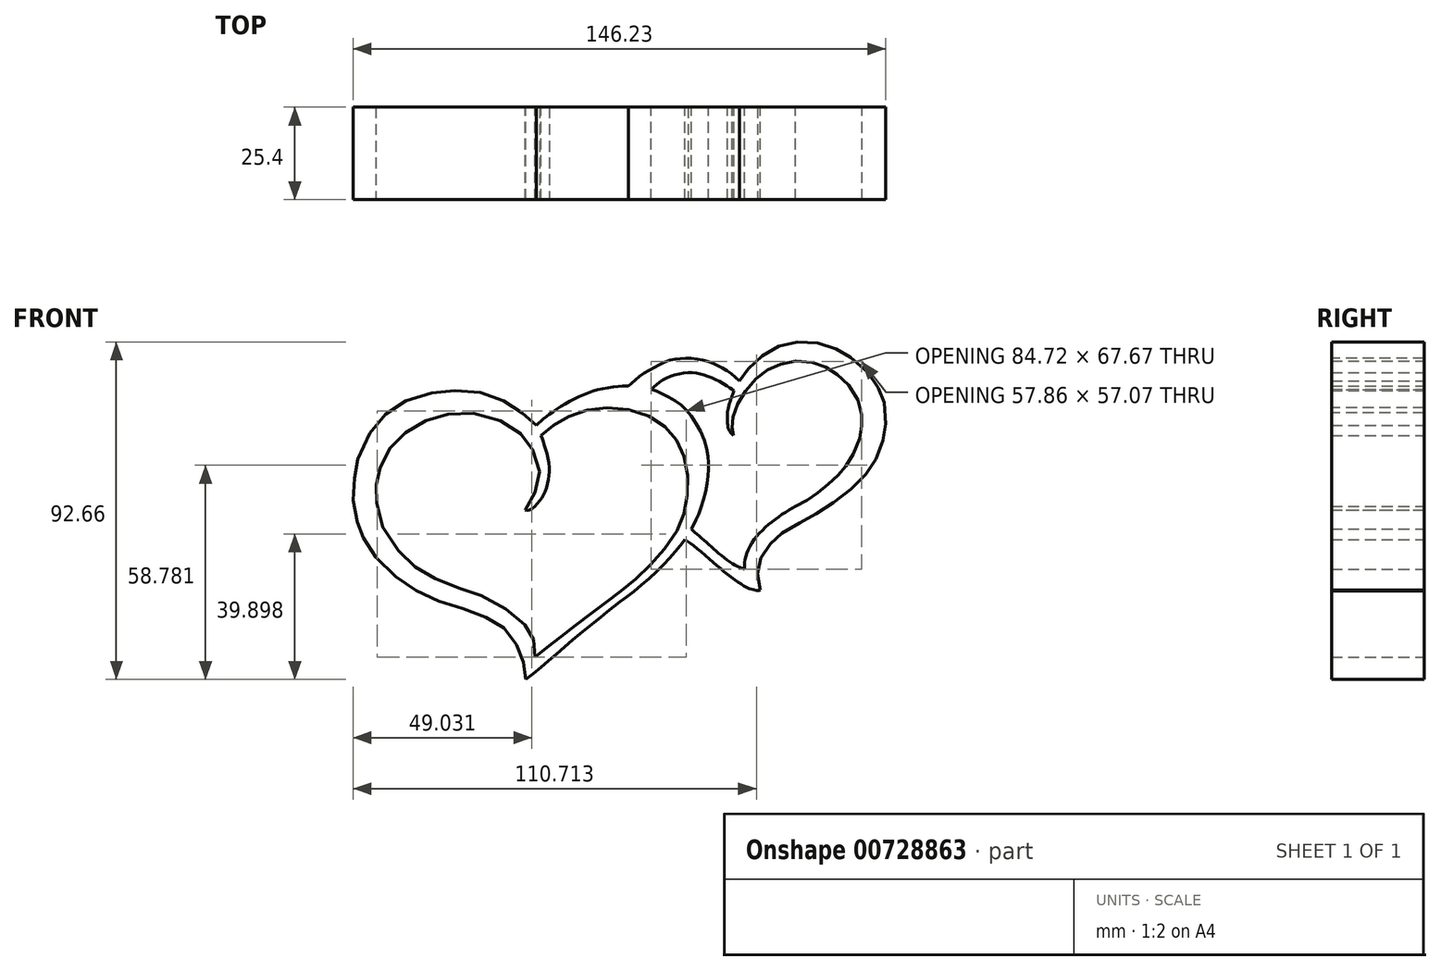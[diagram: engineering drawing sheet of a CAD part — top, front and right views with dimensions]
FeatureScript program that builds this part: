
annotation { "Feature Type Name" : "Feature", "Feature Type Description" : "" }
export const myFeature = defineFeature(function(context is Context, id is Id, definition is map)
    precondition{}
    {
        {
            var Q0;
            Q0=qCreatedBy(makeId("Front.planeOp"),FACE);
            var sketch = newSketch(context, id + "F0", { "sketchPlane" : qUnion([Q0])});
            skFitSpline(sketch, "E0", {"points": [v(-25.48, -6.95) * mm, v(-23.3, -3.15) * mm, v(-21.9, 1) * mm, v(-21.96, 6.21) * mm, v(-24.36, 11.07) * mm, v(-26.96, 14.24) * mm, v(-32.08, 17.5) * mm, v(-39.9, 19.6) * mm, v(-46.56, 19.44) * mm, v(-52.09, 17.95) * mm, v(-57.16, 15.21) * mm, v(-61.5, 11.53) * mm, v(-64.13, 7.75) * mm, v(-65.87, 2.87) * mm, v(-66.37, 0.47) * mm, v(-66.49, -2.24) * mm, v(-66, -7) * mm, v(-63.53, -13.83) * mm, v(-58.46, -20.09) * mm, v(-54.88, -23.15) * mm, v(-49.77, -26) * mm, v(-43.24, -28.5) * mm, v(-37.8, -30.35) * mm, v(-30.6, -34.2) * mm, v(-25.75, -38.22) * mm, v(-23.83, -40.9) * mm, v(-22.82, -44.16) * mm, v(-22.82, -47.34) * mm], "startDerivative": vector(68.52, 110.6) * mm, "endDerivative": vector(-7.66, -109.37) * mm});
            skFitSpline(sketch, "E1", {"points": [v(-22.82, -47.34) * mm, v(-18.93, -44.14) * mm, v(-13.48, -40) * mm, v(-7.44, -35.27) * mm, v(-1.64, -31) * mm, v(4.4, -26.15) * mm, v(10.3, -20.35) * mm, v(16.35, -12.19) * mm, v(18.6, -5.56) * mm, v(19.07, 2.49) * mm, v(17.41, 9.6) * mm, v(13.86, 15.03) * mm, v(7.23, 19.41) * mm, v(-2, 21.19) * mm, v(-10.29, 20) * mm, v(-16.91, 16.93) * mm, v(-21.17, 13.5) * mm], "startDerivative": vector(72.44, 60.92) * mm, "endDerivative": vector(-73.73, -66.23) * mm});
            skFitSpline(sketch, "E2", {"points": [v(-21.17, 13.5) * mm, v(-20.23, 10.77) * mm, v(-19.04, 5.68) * mm, v(-19.16, 1.3) * mm, v(-20.44, -2.66) * mm, v(-22.15, -5.12) * mm, v(-24.41, -6.92) * mm, v(-25.48, -6.95) * mm], "startDerivative": vector(6.78, -18.26) * mm, "endDerivative": vector(-12.06, 2.23) * mm});
            skFitSpline(sketch, "E3", {"points": [v(-22.49, 16.4) * mm, v(-21, 17.67) * mm, v(-18.66, 19.53) * mm, v(-14.77, 22.08) * mm, v(-9.66, 24.67) * mm, v(-4.8, 26.3) * mm, v(0.63, 27.06) * mm, v(2.8, 27.14) * mm], "startDerivative": vector(14.02, 12) * mm, "endDerivative": vector(17.69, 0.26) * mm});
            skFitSpline(sketch, "E4", {"points": [v(2.8, 27.14) * mm, v(4.52, 28.56) * mm, v(7.03, 30.62) * mm, v(10.05, 32.29) * mm, v(13.48, 34.02) * mm, v(16.24, 34.56) * mm, v(19.38, 34.73) * mm, v(22.94, 34.35) * mm, v(25.78, 33.52) * mm, v(28.38, 32.17) * mm, v(30.84, 30.63) * mm, v(33.23, 28.49) * mm], "startDerivative": vector(21.34, 17.25) * mm, "endDerivative": vector(25.3, -24.57) * mm});
            skFitSpline(sketch, "E5", {"points": [v(33.23, 28.49) * mm, v(34.32, 30) * mm, v(36.28, 32.51) * mm, v(38.88, 34.94) * mm, v(42.35, 37.33) * mm, v(45.7, 38.58) * mm, v(49.38, 39.21) * mm, v(53.78, 39.09) * mm, v(57.58, 38.2) * mm, v(61.1, 36.7) * mm, v(63.07, 35.53) * mm, v(67.25, 32.22) * mm, v(69.76, 29.16) * mm, v(71.69, 26.02) * mm, v(72.7, 23.46) * mm, v(73.32, 21.07) * mm, v(73.32, 15.2) * mm, v(72.86, 12.99) * mm, v(71.85, 9.55) * mm, v(70.05, 5.87) * mm, v(68.09, 3.1) * mm, v(65.28, 0) * mm, v(61.4, -3.26) * mm, v(57.42, -5.9) * mm, v(53.94, -8.12) * mm, v(50.64, -10) * mm, v(46.75, -12.14) * mm, v(43.9, -13.94) * mm, v(42.18, -15.66) * mm, v(40.22, -18.1) * mm, v(38.88, -20.9) * mm, v(38.33, -23.41) * mm, v(38.33, -25.93) * mm, v(39, -28.9) * mm], "startDerivative": vector(45.84, 63.78) * mm, "endDerivative": vector(29.25, -107.53) * mm});
            skFitSpline(sketch, "E6", {"points": [v(39, -28.9) * mm, v(38.47, -29.07) * mm, v(35.57, -28.3) * mm, v(33.64, -27.19) * mm, v(30.04, -24.57) * mm, v(26, -21.15) * mm, v(21.03, -16.96) * mm, v(18.28, -15.02) * mm], "startDerivative": vector(-6.74, -4.17) * mm, "endDerivative": vector(-17.62, 11.67) * mm});
            skFitSpline(sketch, "E7", {"points": [v(18.28, -15.02) * mm, v(14.97, -19.19) * mm, v(9.76, -24.52) * mm, v(3.25, -30.03) * mm, v(-1.42, -33.58) * mm, v(-6.16, -37.44) * mm, v(-11.66, -41.82) * mm, v(-18.94, -48.22) * mm, v(-25.38, -53.4) * mm], "startDerivative": vector(-28.94, -38.14) * mm, "endDerivative": vector(-47.2, -36.75) * mm});
            skFitSpline(sketch, "E8", {"points": [v(-25.38, -53.4) * mm, v(-25.4, -52.75) * mm, v(-26.15, -47.9) * mm, v(-27.6, -44.52) * mm, v(-29.98, -40.73) * mm, v(-33.17, -37.94) * mm, v(-37.9, -35.65) * mm, v(-44.12, -33.5) * mm, v(-50.49, -31.42) * mm, v(-56.46, -28.43) * mm, v(-61.58, -24.7) * mm, v(-67.3, -18.81) * mm, v(-70.07, -14.4) * mm, v(-71.16, -11.76) * mm, v(-72.12, -8.39) * mm, v(-72.77, -2.46) * mm, v(-72.37, 2.27) * mm, v(-71.87, 5.76) * mm, v(-68.79, 13.13) * mm, v(-64.66, 18.56) * mm, v(-60.08, 22.1) * mm, v(-52.52, 24.99) * mm, v(-47, 25.79) * mm, v(-40.37, 25.84) * mm, v(-33.85, 24.14) * mm, v(-28.78, 21.55) * mm, v(-25.05, 18.69) * mm, v(-22.49, 16.4) * mm], "startDerivative": vector(-0.57, 35.75) * mm, "endDerivative": vector(80.97, -73.97) * mm});
            skFitSpline(sketch, "E9", {"points": [v(9.01, 26.23) * mm, v(11.44, 28.2) * mm, v(15, 30.03) * mm, v(19.71, 30.8) * mm, v(23.16, 30.28) * mm, v(27.03, 28.8) * mm, v(30.4, 26.8) * mm, v(31.78, 25.88) * mm], "startDerivative": vector(17.08, 14.95) * mm, "endDerivative": vector(12.42, -8.37) * mm});
            skFitSpline(sketch, "E10", {"points": [v(31.78, 25.88) * mm, v(31.08, 23.9) * mm, v(30.2, 21.05) * mm, v(29.95, 18.4) * mm, v(30.3, 15.34) * mm, v(31.63, 13.58) * mm], "startDerivative": vector(-3.7, -10.34) * mm, "endDerivative": vector(8.41, -8.35) * mm});
            skFitSpline(sketch, "E11", {"points": [v(31.63, 13.58) * mm, v(31.32, 14.99) * mm, v(31.3, 17.05) * mm, v(32.2, 20.97) * mm, v(34.89, 25.6) * mm, v(39.12, 30.28) * mm, v(43.2, 32.65) * mm, v(49, 34.01) * mm, v(54.86, 33.18) * mm, v(58.92, 31.14) * mm, v(63.31, 27.26) * mm, v(66.6, 21.03) * mm, v(66.85, 17.1) * mm, v(66.6, 14.1) * mm, v(64.26, 8.03) * mm, v(61.82, 4.34) * mm, v(59.23, 1.6) * mm, v(55.75, -1.44) * mm, v(52.22, -3.98) * mm, v(48.68, -5.92) * mm], "startDerivative": vector(-11.81, 45.6) * mm, "endDerivative": vector(-68.5, -30.39) * mm});
            skFitSpline(sketch, "E12", {"points": [v(48.68, -5.92) * mm, v(44.85, -8.21) * mm, v(40.67, -11.45) * mm, v(37.29, -15.04) * mm, v(35.25, -18.97) * mm, v(34.65, -21.56) * mm, v(34.65, -23.16) * mm], "startDerivative": vector(-20.93, -11.74) * mm, "endDerivative": vector(0.69, -14.02) * mm});
            skFitSpline(sketch, "E13", {"points": [v(34.65, -23.16) * mm, v(31.81, -21.86) * mm, v(27.63, -18.82) * mm, v(24, -15.58) * mm, v(20.97, -13) * mm, v(20.07, -12.15) * mm], "startDerivative": vector(-14.38, 5.6) * mm, "endDerivative": vector(-6.28, 6.24) * mm});
            skFitSpline(sketch, "E14", {"points": [v(20.07, -12.15) * mm, v(21.06, -10.1) * mm, v(22.56, -6.77) * mm, v(24.1, -1.14) * mm, v(24.75, 3.9) * mm, v(24.65, 7.43) * mm, v(23.15, 13.5) * mm, v(19.52, 19.49) * mm, v(16.14, 22.72) * mm, v(12, 25.06) * mm, v(9.01, 26.23) * mm], "startDerivative": vector(13.35, 27.52) * mm, "endDerivative": vector(-33.88, 11.96) * mm});
            skSolve(sketch);
        }
        {
            var Q0;
            Q0=makeQuery(id+"F0.imprint","IMPRINT",FACE,{"disambiguationData":[TD([[makeQuery(id+"F0.imprint","IMPRINT",EDGE,{"derivedFrom":sQuery(id+"F0.wireOp",EDGE,"E0")}),-1.0]])]});
            extrude(context, id + "F1", {"entities" : qUnion([Q0]), "depth" : 25.4 * mm, "offsetDistance" : 25.4 * mm});
        }
    });
